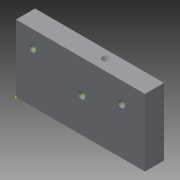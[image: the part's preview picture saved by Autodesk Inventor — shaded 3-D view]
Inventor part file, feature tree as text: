
AUTODESK INVENTOR PART (.ipt)
format: ipt  version: 2015 (Build 190159000, 159)  size: 83,968 bytes
history: native  units: in
note: dims shown in document units (in); Inventor stores cm internally (conversion verified against a paired STEP export)
features: sketch x3, hole x2, extrude x1
ambient origin geometry x8: Origin, YZ Plane, XZ Plane, XY Plane, X Axis, Y Axis, Z Axis, Center Point
bodies: Solid1 (feature_tree)
feature tree (6):
  extrude  "Extrusion1"  Depth=1.0in
  hole  "Hole1"  [1 undecoded]
  sketch  "Sketch2"  dims[d4=0.1in d5=0.25in d6=0.375in d7=0.25in d8=0.5635in d9=0.375in d10=0.8108in]
  sketch  "Sketch3"  dims[d11=0.1in d12=0.25in d13=0.375in d14=0.25in d15=0.5635in d16=0.375in d17=0.8108in]
  hole  "Hole2"  [1 undecoded]
  sketch  "Sketch1"  dims[d0=1.0in d1=0.0in d2=1.0in d3=1.0in]
note: 2 required parameter values undecoded (feature->parameter linkage not recoverable at this tier; creation-order binding heuristic only, values carry confidence <= 0.55)
